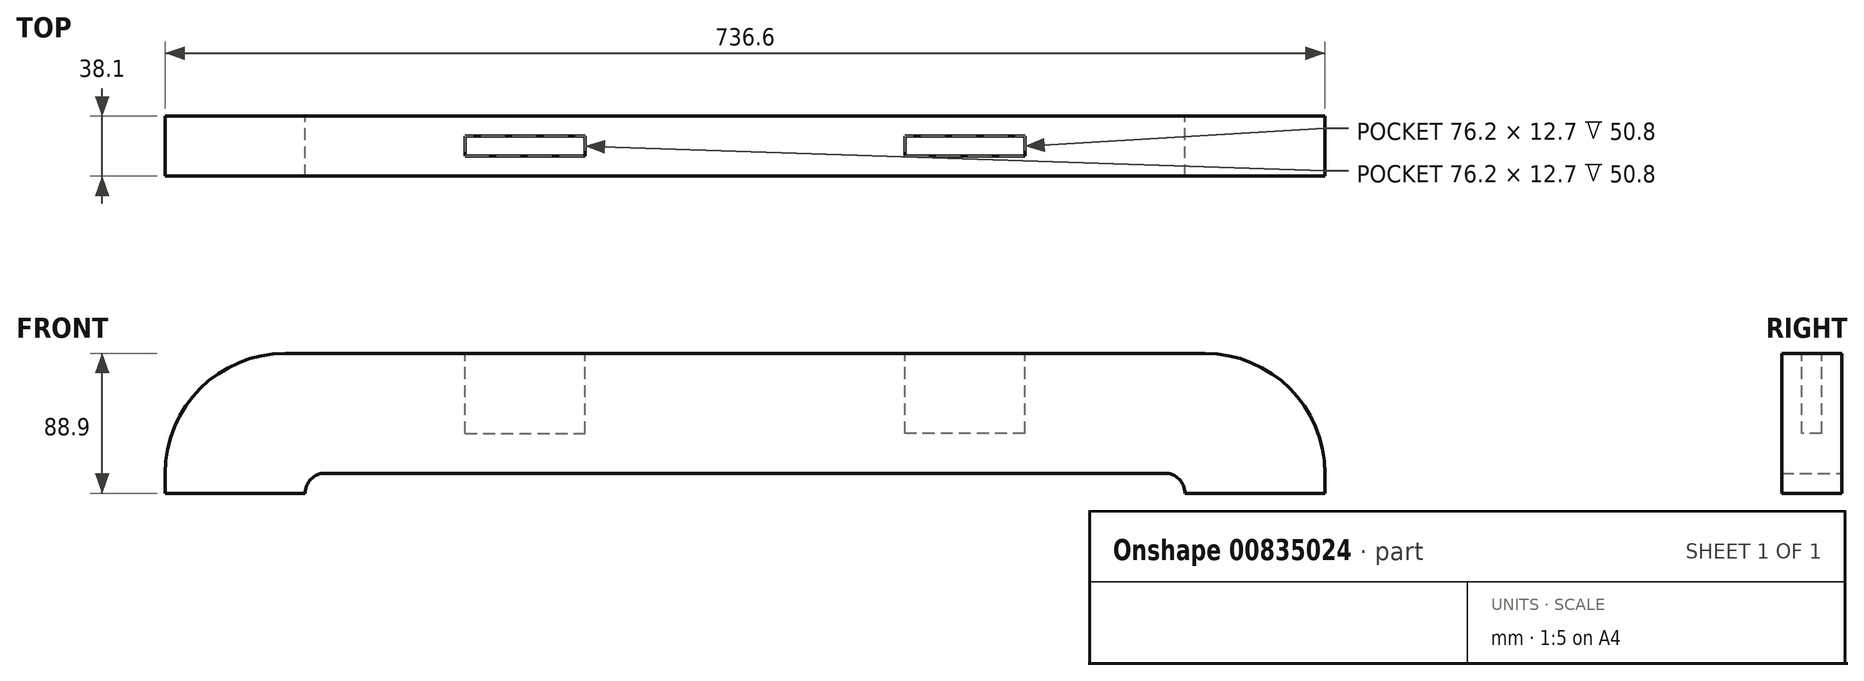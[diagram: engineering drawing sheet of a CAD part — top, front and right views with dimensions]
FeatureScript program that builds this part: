
annotation { "Feature Type Name" : "Feature", "Feature Type Description" : "" }
export const myFeature = defineFeature(function(context is Context, id is Id, definition is map)
    precondition{}
    {
        {
            var Q0;
            Q0=qCreatedBy(makeId("Front.planeOp"),FACE);
            var sketch = newSketch(context, id + "F0", { "sketchPlane" : qUnion([Q0])});
            skLineSegment(sketch, "E0.bottom", {"start": v(-368.3, 0) * mm, "end": v(-279.4, 0) * mm});
            skLineSegment(sketch, "E0.top", {"start": v(-292.1, 88.9) * mm, "end": v(292.1, 88.9) * mm});
            skLineSegment(sketch, "E0.left", {"start": v(-368.3, 0) * mm, "end": v(-368.3, 12.7) * mm});
            skLineSegment(sketch, "E0.right", {"start": v(368.3, 0) * mm, "end": v(368.3, 12.7) * mm});
            skArc(sketch, "E1.filletArc", {"start": v(-292.1, 88.9) * mm, "mid": v(-345.98, 66.58) * mm, "end": v(-368.3, 12.7) * mm});
            skArc(sketch, "E2.MirrorCS", {"start": v(292.1, 88.9) * mm, "mid": v(345.98, 66.58) * mm, "end": v(368.3, 12.7) * mm});
            skLineSegment(sketch, "E3.top", {"start": v(-266.7, 12.7) * mm, "end": v(266.7, 12.7) * mm});
            skLineSegment(sketch, "E4.trimOffspring", {"start": v(279.4, 0) * mm, "end": v(368.3, 0) * mm});
            skArc(sketch, "E5", {"start": v(-266.7, 12.7) * mm, "mid": v(-275.68, 8.98) * mm, "end": v(-279.4, 0) * mm});
            skArc(sketch, "E6.MirrorCS", {"start": v(266.7, 12.7) * mm, "mid": v(275.68, 8.98) * mm, "end": v(279.4, 0) * mm});
            skSolve(sketch);
        }
        {
            var Q0;
            Q0 = qSketchRegion(id + "F0", true);
            extrude(context, id + "F1", {"entities" : qUnion([Q0]), "depth" : 38.1 * mm, "offsetDistance" : 25.4 * mm});
        }
        {
            var Q0;
            Q0=makeQuery(id+"F1.opExtrude","SWEPT_FACE",FACE,{"disambiguationData":[OSD([sQuery(id+"F0.wireOp",EDGE,"E0.top")])]});
            var sketch = newSketch(context, id + "F2", { "sketchPlane" : qUnion([Q0])});
            skLineSegment(sketch, "E7.bottom", {"start": v(-177.8, -12.7) * mm, "end": v(-101.6, -12.7) * mm});
            skLineSegment(sketch, "E7.top", {"start": v(-177.8, -25.4) * mm, "end": v(-101.6, -25.4) * mm});
            skLineSegment(sketch, "E7.left", {"start": v(-177.8, -12.7) * mm, "end": v(-177.8, -25.4) * mm});
            skLineSegment(sketch, "E7.right", {"start": v(-101.6, -12.7) * mm, "end": v(-101.6, -25.4) * mm});
            skPoint(sketch, "E8", {"position": v(-101.6, -19.05) * mm});
            skLineSegment(sketch, "E9.MirrorCS", {"start": v(101.6, -12.7) * mm, "end": v(101.6, -25.4) * mm});
            skLineSegment(sketch, "E10.MirrorCS", {"start": v(177.8, -12.7) * mm, "end": v(177.8, -25.4) * mm});
            skLineSegment(sketch, "E11.MirrorCS", {"start": v(177.8, -12.7) * mm, "end": v(101.6, -12.7) * mm});
            skLineSegment(sketch, "E12.MirrorCS", {"start": v(177.8, -25.4) * mm, "end": v(101.6, -25.4) * mm});
            skSolve(sketch);
        }
        {
            var Q0;
            Q0 = qSketchRegion(id + "F2", true);
            extrude(context, id + "F3", {"entities" : qUnion([Q0]), "operationType" : NewBodyOperationType.REMOVE, "oppositeDirection" : true, "depth" : 50.8 * mm, "offsetDistance" : 25.4 * mm});
        }
    });
